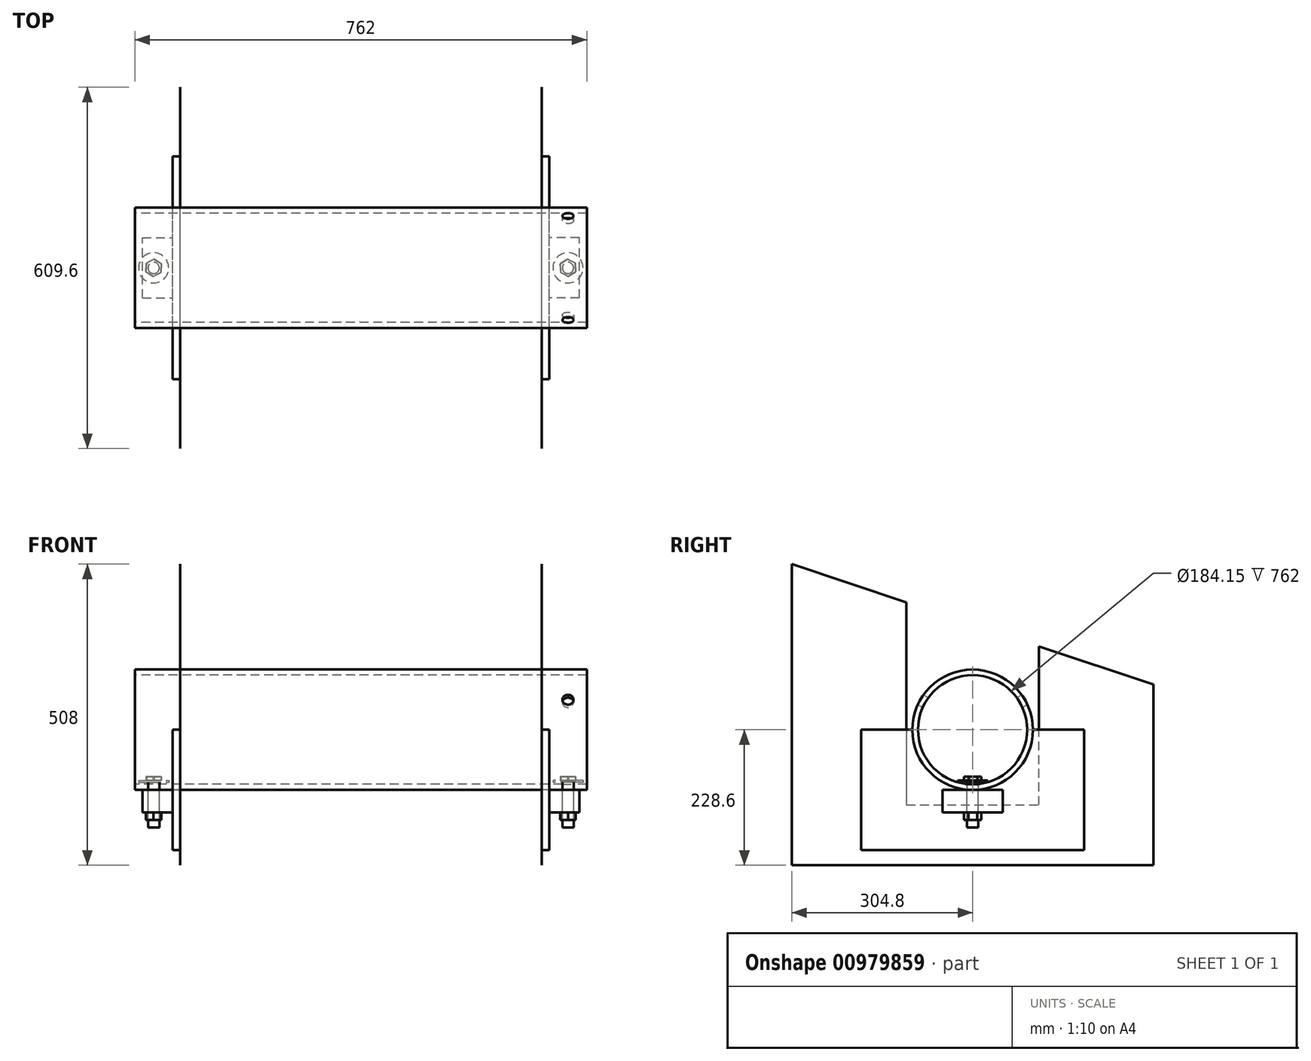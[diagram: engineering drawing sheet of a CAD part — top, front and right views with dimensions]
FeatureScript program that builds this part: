
annotation { "Feature Type Name" : "Feature", "Feature Type Description" : "" }
export const myFeature = defineFeature(function(context is Context, id is Id, definition is map)
    precondition{}
    {
        {
            var Q0;
            Q0=qCreatedBy(makeId("Right.planeOp"),FACE);
            cPlane(context, id + "F0", {"entities" : qUnion([Q0]), "cplaneType" : CPlaneType.OFFSET, "offset" : 304.8 * mm, "width" : 152.4 * mm, "height" : 152.4 * mm});
        }
        {
            var Q0;
            Q0=qCreatedBy(makeId("Right.planeOp"),FACE);
            var sketch = newSketch(context, id + "F1", { "sketchPlane" : qUnion([Q0])});
            skCircle(sketch, "E0", {"center": v(0, 0) * mm, "radius": 101.6 * mm});
            skCircle(sketch, "E1.0", {"center": v(0, 0) * mm, "radius": 92.08 * mm});
            skSolve(sketch);
        }
        {
            var Q0;
            Q0=qCreatedBy(id+"F0.planeOp",FACE);
            var sketch = newSketch(context, id + "F2", { "sketchPlane" : qUnion([Q0])});
            skLineSegment(sketch, "E2", {"start": v(-152.4, -228.6) * mm, "end": v(152.4, -228.6) * mm});
            skLineSegment(sketch, "E3", {"start": v(152.4, -228.6) * mm, "end": v(152.4, 127) * mm});
            skLineSegment(sketch, "E4", {"start": v(152.4, 127) * mm, "end": v(-152.4, 228.6) * mm});
            skLineSegment(sketch, "E5", {"start": v(-152.4, 228.6) * mm, "end": v(-152.4, -228.6) * mm});
            skLineSegment(sketch, "E6", {"start": v(0, -228.6) * mm, "end": v(0, 0) * mm, "construction": true});
            skLineSegment(sketch, "E7", {"start": v(0, 0) * mm, "end": v(-152.4, 0) * mm, "construction": true});
            skLineSegment(sketch, "E8.0", {"start": v(111.76, -127) * mm, "end": v(111.76, 140.55) * mm});
            skLineSegment(sketch, "E8.1", {"start": v(-111.76, -127) * mm, "end": v(111.76, -127) * mm});
            skLineSegment(sketch, "E8.2", {"start": v(-111.76, 215.05) * mm, "end": v(-111.76, -127) * mm});
            skLineSegment(sketch, "E9", {"start": v(-152.4, 228.6) * mm, "end": v(-304.8, 279.4) * mm});
            skLineSegment(sketch, "E10", {"start": v(-304.8, 279.4) * mm, "end": v(-304.8, -228.6) * mm});
            skLineSegment(sketch, "E11", {"start": v(-304.8, -228.6) * mm, "end": v(-152.4, -228.6) * mm});
            skLineSegment(sketch, "E12", {"start": v(152.4, -228.6) * mm, "end": v(304.8, -228.6) * mm});
            skLineSegment(sketch, "E13", {"start": v(304.8, 76.2) * mm, "end": v(152.4, 127) * mm});
            skLineSegment(sketch, "E14", {"start": v(304.8, -228.6) * mm, "end": v(304.8, 76.2) * mm});
            skSolve(sketch);
        }
        {
            var Q0;
            Q0=makeQuery(id+"F2.imprint","IMPRINT",FACE,{"disambiguationData":[TD([[makeQuery(id+"F2.imprint","IMPRINT",EDGE,{"derivedFrom":sQuery(id+"F2.wireOp",EDGE,"E2")}),1.0]])]});
            var Q1;
            Q1=makeQuery(id+"F2.imprint","IMPRINT",FACE,{"disambiguationData":[TD([[makeQuery(id+"F2.imprint","IMPRINT",EDGE,{"derivedFrom":sQuery(id+"F2.wireOp",EDGE,"E5")}),-1.0]])]});
            var Q2;
            Q2=makeQuery(id+"F2.imprint","IMPRINT",FACE,{"disambiguationData":[TD([[makeQuery(id+"F2.imprint","IMPRINT",EDGE,{"derivedFrom":sQuery(id+"F2.wireOp",EDGE,"E3")}),-1.0]])]});
            extrude(context, id + "F3", {"entities" : qUnion([Q0, Q1, Q2]), "depth" : 1 / 101.6 * mm, "offsetDistance" : 25.4 * mm});
        }
        {
            var Q0;
            Q0=makeQuery(id+"F1.imprint","IMPRINT",FACE,{"disambiguationData":[TD([[makeQuery(id+"F1.imprint","IMPRINT",EDGE,{"derivedFrom":sQuery(id+"F1.wireOp",EDGE,"E0")}),1.0]])]});
            extrude(context, id + "F4", {"entities" : qUnion([Q0]), "endBound" : BoundingType.SYMMETRIC, "depth" : 762 * mm, "offsetDistance" : 25.4 * mm});
        }
        {
            var Q0;
            Q0=makeQuery(id+"F3.opExtrude","CAP_FACE",FACE,{"disambiguationData":[OSD([sQuery(id+"F2.wireOp",EDGE,"E2"),sQuery(id+"F2.wireOp",EDGE,"E4"),sQuery(id+"F2.wireOp",EDGE,"E8.0"),sQuery(id+"F2.wireOp",EDGE,"E8.1"),sQuery(id+"F2.wireOp",EDGE,"E8.2"),sQuery(id+"F2.wireOp",EDGE,"E9"),sQuery(id+"F2.wireOp",EDGE,"E10"),sQuery(id+"F2.wireOp",EDGE,"E11"),sQuery(id+"F2.wireOp",EDGE,"E12"),sQuery(id+"F2.wireOp",EDGE,"E13"),sQuery(id+"F2.wireOp",EDGE,"E14")])],"isStart":false});
            var sketch = newSketch(context, id + "F5", { "sketchPlane" : qUnion([Q0])});
            skArc(sketch, "E15.1", {"start": v(-101.6, 0) * mm, "mid": v(0, -101.6) * mm, "end": v(101.6, 0) * mm});
            skLineSegment(sketch, "E16.0", {"start": v(111.76, -127) * mm, "end": v(111.76, 140.55) * mm});
            skLineSegment(sketch, "E16.1", {"start": v(-111.76, -127) * mm, "end": v(111.76, -127) * mm});
            skLineSegment(sketch, "E16.2", {"start": v(-111.76, 215.05) * mm, "end": v(-111.76, -127) * mm});
            skLineSegment(sketch, "E17.bottom", {"start": v(-187.96, 0) * mm, "end": v(-101.6, 0) * mm});
            skLineSegment(sketch, "E17.top", {"start": v(-187.96, -203.2) * mm, "end": v(187.96, -203.2) * mm});
            skLineSegment(sketch, "E17.left", {"start": v(-187.96, 0) * mm, "end": v(-187.96, -203.2) * mm});
            skLineSegment(sketch, "E17.right", {"start": v(187.96, 0) * mm, "end": v(187.96, -203.2) * mm});
            skLineSegment(sketch, "E18", {"start": v(0, -203.2) * mm, "end": v(0, 0) * mm, "construction": true});
            skLineSegment(sketch, "E19.trimOffspring", {"start": v(101.6, 0) * mm, "end": v(187.96, 0) * mm});
            skSolve(sketch);
        }
        {
            var Q0;
            Q0 = qSketchRegion(id + "F5", true);
            extrude(context, id + "F6", {"entities" : qUnion([Q0]), "depth" : 12.7 * mm, "offsetDistance" : 25.4 * mm});
        }
        {
            var Q0;
            Q0=makeQuery(id+"F6.opExtrude","CAP_FACE",FACE,{"disambiguationData":[OSD([sQuery(id+"F5.wireOp",EDGE,"E15.1"),sQuery(id+"F5.wireOp",EDGE,"E17.bottom"),sQuery(id+"F5.wireOp",EDGE,"E17.top"),sQuery(id+"F5.wireOp",EDGE,"E17.left"),sQuery(id+"F5.wireOp",EDGE,"E17.right"),sQuery(id+"F5.wireOp",EDGE,"E19.trimOffspring")])],"isStart":false});
            var sketch = newSketch(context, id + "F7", { "sketchPlane" : qUnion([Q0])});
            skCircle(sketch, "E20.0", {"center": v(0, 0) * mm, "radius": 101.6 * mm});
            skLineSegment(sketch, "E21", {"start": v(0, -101.6) * mm, "end": v(50.8, -101.6) * mm});
            skLineSegment(sketch, "E22", {"start": v(50.8, -101.6) * mm, "end": v(50.8, -139.7) * mm});
            skLineSegment(sketch, "E23", {"start": v(50.8, -139.7) * mm, "end": v(-50.8, -139.7) * mm});
            skLineSegment(sketch, "E24", {"start": v(-50.8, -139.7) * mm, "end": v(-50.8, -101.6) * mm});
            skLineSegment(sketch, "E25", {"start": v(-50.8, -101.6) * mm, "end": v(0, -101.6) * mm});
            skSolve(sketch);
        }
        {
            var Q0;
            Q0=makeQuery(id+"F7.imprint","IMPRINT",FACE,{"disambiguationData":[TD([[makeQuery(id+"F7.imprint","IMPRINT",EDGE,{"derivedFrom":sQuery(id+"F7.wireOp",EDGE,"E21")}),-1.0]])]});
            extrude(context, id + "F8", {"entities" : qUnion([Q0]), "depth" : 50.8 * mm, "offsetDistance" : 25.4 * mm});
        }
        {
            var Q0;
            Q0=makeQuery(id+"F8.opExtrude","SWEPT_FACE",FACE,{"disambiguationData":[OSD([sQuery(id+"F7.wireOp",EDGE,"E21"),sQuery(id+"F7.wireOp",EDGE,"E25")])]});
            var sketch = newSketch(context, id + "F9", { "sketchPlane" : qUnion([Q0])});
            skLineSegment(sketch, "E26", {"start": v(349.25, -50.8) * mm, "end": v(349.25, 50.8) * mm, "construction": true});
            skPoint(sketch, "E27", {"position": v(349.25, 0) * mm});
            skCircle(sketch, "E28", {"center": v(349.25, 0) * mm, "radius": 9.53 * mm});
            skSolve(sketch);
        }
        {
            var Q0;
            Q0=makeQuery(id+"F9.imprint","IMPRINT",FACE,{"disambiguationData":[TD([[makeQuery(id+"F9.imprint","IMPRINT",EDGE,{"derivedFrom":sQuery(id+"F9.wireOp",EDGE,"E28")}),1.0]])]});
            extrude(context, id + "F10", {"entities" : qUnion([Q0]), "operationType" : NewBodyOperationType.REMOVE, "endBound" : BoundingType.UP_TO_NEXT, "oppositeDirection" : true, "depth" : 25.4 * mm, "offsetDistance" : 25.4 * mm});
        }
        {
            var Q0;
            Q0 = qSketchRegion(id + "F9", true);
            extrude(context, id + "F11", {"entities" : qUnion([Q0]), "endBound" : BoundingType.UP_TO_NEXT, "depth" : 25.4 * mm, "offsetDistance" : 25.4 * mm});
        }
        {
            var Q0;
            Q0=makeQuery(id+"F11.opExtrude","SWEPT_BODY",BODY,{"disambiguationData":[OSD([sQuery(id+"F9.wireOp",EDGE,"E28")])]});
            var Q1;
            Q1=makeQuery(id+"F4.opExtrude","SWEPT_FACE",FACE,{"disambiguationData":[OSD([sQuery(id+"F1.wireOp",EDGE,"E1.0")])]});
            circularPattern(context, id + "F12", {"operationType" : NewBodyOperationType.REMOVE, "entities" : qUnion([Q0]), "axis" : qUnion([Q1]), "angle" : 360 * degree, "instanceCount" : 3, "equalSpace" : true});
        }
        {
            var Q0;
            Q0=makeQuery(id+"F8.opExtrude","SWEPT_FACE",FACE,{"disambiguationData":[OSD([sQuery(id+"F7.wireOp",EDGE,"E21"),sQuery(id+"F7.wireOp",EDGE,"E25")])]});
            cPlane(context, id + "F13", {"entities" : qUnion([Q0]), "cplaneType" : CPlaneType.OFFSET, "offset" : 12.7 * mm, "width" : 152.4 * mm, "height" : 152.4 * mm});
        }
        {
            var Q0;
            Q0=qCreatedBy(id+"F13.planeOp",FACE);
            var sketch = newSketch(context, id + "F14", { "sketchPlane" : qUnion([Q0])});
            skCircle(sketch, "E29.0", {"center": v(349.25, 0) * mm, "radius": 9.53 * mm});
            skSolve(sketch);
        }
        {
            var Q0;
            Q0=makeQuery(id+"F14.imprint","IMPRINT",FACE,{"disambiguationData":[TD([[makeQuery(id+"F14.imprint","IMPRINT",EDGE,{"derivedFrom":sQuery(id+"F14.wireOp",EDGE,"E29.0")}),1.0]])]});
            extrude(context, id + "F15", {"entities" : qUnion([Q0]), "oppositeDirection" : true, "depth" : 76.2 * mm, "offsetDistance" : 25.4 * mm});
        }
        {
            var Q0;
            Q0=makeQuery(id+"F15.opExtrude","CAP_FACE",FACE,{"disambiguationData":[OSD([sQuery(id+"F14.wireOp",EDGE,"E29.0")])],"isStart":true});
            var sketch = newSketch(context, id + "F16", { "sketchPlane" : qUnion([Q0])});
            skCircle(sketch, "E30", {"center": v(349.25, 0) * mm, "radius": 25.4 * mm});
            skCircle(sketch, "E31.0", {"center": v(349.25, 0) * mm, "radius": 9.53 * mm});
            skSolve(sketch);
        }
        {
            var Q0;
            Q0=makeQuery(id+"F16.imprint","IMPRINT",FACE,{"disambiguationData":[TD([[makeQuery(id+"F16.imprint","IMPRINT",EDGE,{"derivedFrom":sQuery(id+"F16.wireOp",EDGE,"E30")}),1.0]])]});
            extrude(context, id + "F17", {"entities" : qUnion([Q0]), "depth" : 3.17 * mm, "offsetDistance" : 25.4 * mm});
        }
        {
            var Q0;
            Q0=makeQuery(id+"F15.opExtrude","CAP_FACE",FACE,{"disambiguationData":[OSD([sQuery(id+"F14.wireOp",EDGE,"E29.0")])],"isStart":true});
            extrude(context, id + "F18", {"entities" : qUnion([Q0]), "operationType" : NewBodyOperationType.ADD, "depth" : 6.35 * mm, "offsetDistance" : 25.4 * mm});
        }
        {
            var Q0;
            Q0=makeQuery(id+"F17.opExtrude","CAP_FACE",FACE,{"disambiguationData":[OSD([sQuery(id+"F16.wireOp",EDGE,"E30"),sQuery(id+"F16.wireOp",EDGE,"E31.0")])],"isStart":false});
            var sketch = newSketch(context, id + "F19", { "sketchPlane" : qUnion([Q0])});
            skCircle(sketch, "E32.0", {"center": v(349.25, 0) * mm, "radius": 9.53 * mm});
            skCircle(sketch, "E33.cCircle", {"center": v(349.25, 0) * mm, "radius": 12.7 * mm, "construction": true});
            skLineSegment(sketch, "E33.0", {"start": v(348.08, 14.62) * mm, "end": v(361.32, 8.32) * mm});
            skLineSegment(sketch, "E33.1", {"start": v(361.32, 8.32) * mm, "end": v(362.5, -6.3) * mm});
            skLineSegment(sketch, "E33.2", {"start": v(362.5, -6.3) * mm, "end": v(350.42, -14.62) * mm});
            skLineSegment(sketch, "E33.3", {"start": v(350.42, -14.62) * mm, "end": v(337.18, -8.32) * mm});
            skLineSegment(sketch, "E33.4", {"start": v(337.18, -8.32) * mm, "end": v(336, 6.3) * mm});
            skLineSegment(sketch, "E33.5", {"start": v(336, 6.3) * mm, "end": v(348.08, 14.62) * mm});
            skPoint(sketch, "E33.0.midPoint", {"position": v(354.7, 11.47) * mm});
            skSolve(sketch);
        }
        {
            var Q0;
            Q0=makeQuery(id+"F19.imprint","IMPRINT",FACE,{"disambiguationData":[TD([[makeQuery(id+"F19.imprint","IMPRINT",EDGE,{"derivedFrom":sQuery(id+"F19.wireOp",EDGE,"E32.0")}),-1.0]])]});
            var Q1;
            Q1=makeQuery(id+"F19.imprint","IMPRINT",FACE,{"disambiguationData":[TD([[makeQuery(id+"F19.imprint","IMPRINT",EDGE,{"derivedFrom":sQuery(id+"F19.wireOp",EDGE,"E32.0")}),1.0]])]});
            extrude(context, id + "F20", {"entities" : qUnion([Q0, Q1]), "operationType" : NewBodyOperationType.ADD, "depth" : 6.35 * mm, "offsetDistance" : 25.4 * mm});
        }
        {
            var Q0;
            Q0=makeQuery(id+"F8.opExtrude","SWEPT_FACE",FACE,{"disambiguationData":[OSD([sQuery(id+"F7.wireOp",EDGE,"E23")])]});
            var sketch = newSketch(context, id + "F21", { "sketchPlane" : qUnion([Q0])});
            skCircle(sketch, "E34.0", {"center": v(349.25, 0) * mm, "radius": 9.53 * mm});
            skCircle(sketch, "E35.cCircle", {"center": v(349.25, 0) * mm, "radius": 12.7 * mm, "construction": true});
            skLineSegment(sketch, "E35.0", {"start": v(361.76, -7.65) * mm, "end": v(348.88, -14.66) * mm});
            skLineSegment(sketch, "E35.1", {"start": v(348.88, -14.66) * mm, "end": v(336.37, -7) * mm});
            skLineSegment(sketch, "E35.2", {"start": v(336.37, -7) * mm, "end": v(336.74, 7.65) * mm});
            skLineSegment(sketch, "E35.3", {"start": v(336.74, 7.65) * mm, "end": v(349.62, 14.66) * mm});
            skLineSegment(sketch, "E35.4", {"start": v(349.62, 14.66) * mm, "end": v(362.13, 7) * mm});
            skLineSegment(sketch, "E35.5", {"start": v(362.13, 7) * mm, "end": v(361.76, -7.65) * mm});
            skPoint(sketch, "E35.0.midPoint", {"position": v(355.32, -11.16) * mm});
            skSolve(sketch);
        }
        {
            var Q0;
            Q0=makeQuery(id+"F21.imprint","IMPRINT",FACE,{"disambiguationData":[TD([[makeQuery(id+"F21.imprint","IMPRINT",EDGE,{"derivedFrom":sQuery(id+"F21.wireOp",EDGE,"E34.0")}),1.0]])]});
            extrude(context, id + "F22", {"entities" : qUnion([Q0]), "depth" : 12.7 * mm, "offsetDistance" : 25.4 * mm});
        }
        {
            var Q0;
            Q0=makeQuery(id+"F3.opExtrude","SWEPT_BODY",BODY,{"disambiguationData":[OSD([sQuery(id+"F2.wireOp",EDGE,"E2"),sQuery(id+"F2.wireOp",EDGE,"E4"),sQuery(id+"F2.wireOp",EDGE,"E8.0"),sQuery(id+"F2.wireOp",EDGE,"E8.1"),sQuery(id+"F2.wireOp",EDGE,"E8.2"),sQuery(id+"F2.wireOp",EDGE,"E9"),sQuery(id+"F2.wireOp",EDGE,"E10"),sQuery(id+"F2.wireOp",EDGE,"E11"),sQuery(id+"F2.wireOp",EDGE,"E12"),sQuery(id+"F2.wireOp",EDGE,"E13"),sQuery(id+"F2.wireOp",EDGE,"E14")])]});
            var Q1;
            Q1=makeQuery(id+"F6.opExtrude","SWEPT_BODY",BODY,{"disambiguationData":[OSD([sQuery(id+"F5.wireOp",EDGE,"E15.1"),sQuery(id+"F5.wireOp",EDGE,"E17.bottom"),sQuery(id+"F5.wireOp",EDGE,"E17.top"),sQuery(id+"F5.wireOp",EDGE,"E17.left"),sQuery(id+"F5.wireOp",EDGE,"E17.right"),sQuery(id+"F5.wireOp",EDGE,"E19.trimOffspring")])]});
            var Q2;
            Q2=makeQuery(id+"F8.opExtrude","SWEPT_BODY",BODY,{"disambiguationData":[OSD([sQuery(id+"F7.wireOp",EDGE,"E21"),sQuery(id+"F7.wireOp",EDGE,"E22"),sQuery(id+"F7.wireOp",EDGE,"E23"),sQuery(id+"F7.wireOp",EDGE,"E24"),sQuery(id+"F7.wireOp",EDGE,"E25")])]});
            var Q3;
            Q3=makeQuery(id+"F15.opExtrude","SWEPT_BODY",BODY,{"disambiguationData":[OSD([sQuery(id+"F14.wireOp",EDGE,"E29.0")])]});
            var Q4;
            Q4=makeQuery(id+"F22.opExtrude","SWEPT_BODY",BODY,{"disambiguationData":[OSD([sQuery(id+"F21.wireOp",EDGE,"E34.0"),sQuery(id+"F21.wireOp",EDGE,"E35.0"),sQuery(id+"F21.wireOp",EDGE,"E35.1"),sQuery(id+"F21.wireOp",EDGE,"E35.2"),sQuery(id+"F21.wireOp",EDGE,"E35.3"),sQuery(id+"F21.wireOp",EDGE,"E35.4"),sQuery(id+"F21.wireOp",EDGE,"E35.5")])]});
            var Q5;
            Q5=makeQuery(id+"F17.opExtrude","SWEPT_BODY",BODY,{"disambiguationData":[OSD([sQuery(id+"F16.wireOp",EDGE,"E30"),sQuery(id+"F16.wireOp",EDGE,"E31.0")])]});
            var Q6;
            Q6=qCreatedBy(makeId("Right.planeOp"),FACE);
            mirror(context, id + "F23", {"entities" : qUnion([Q0, Q1, Q2, Q3, Q4, Q5]), "mirrorPlane" : qUnion([Q6])});
        }
    });
